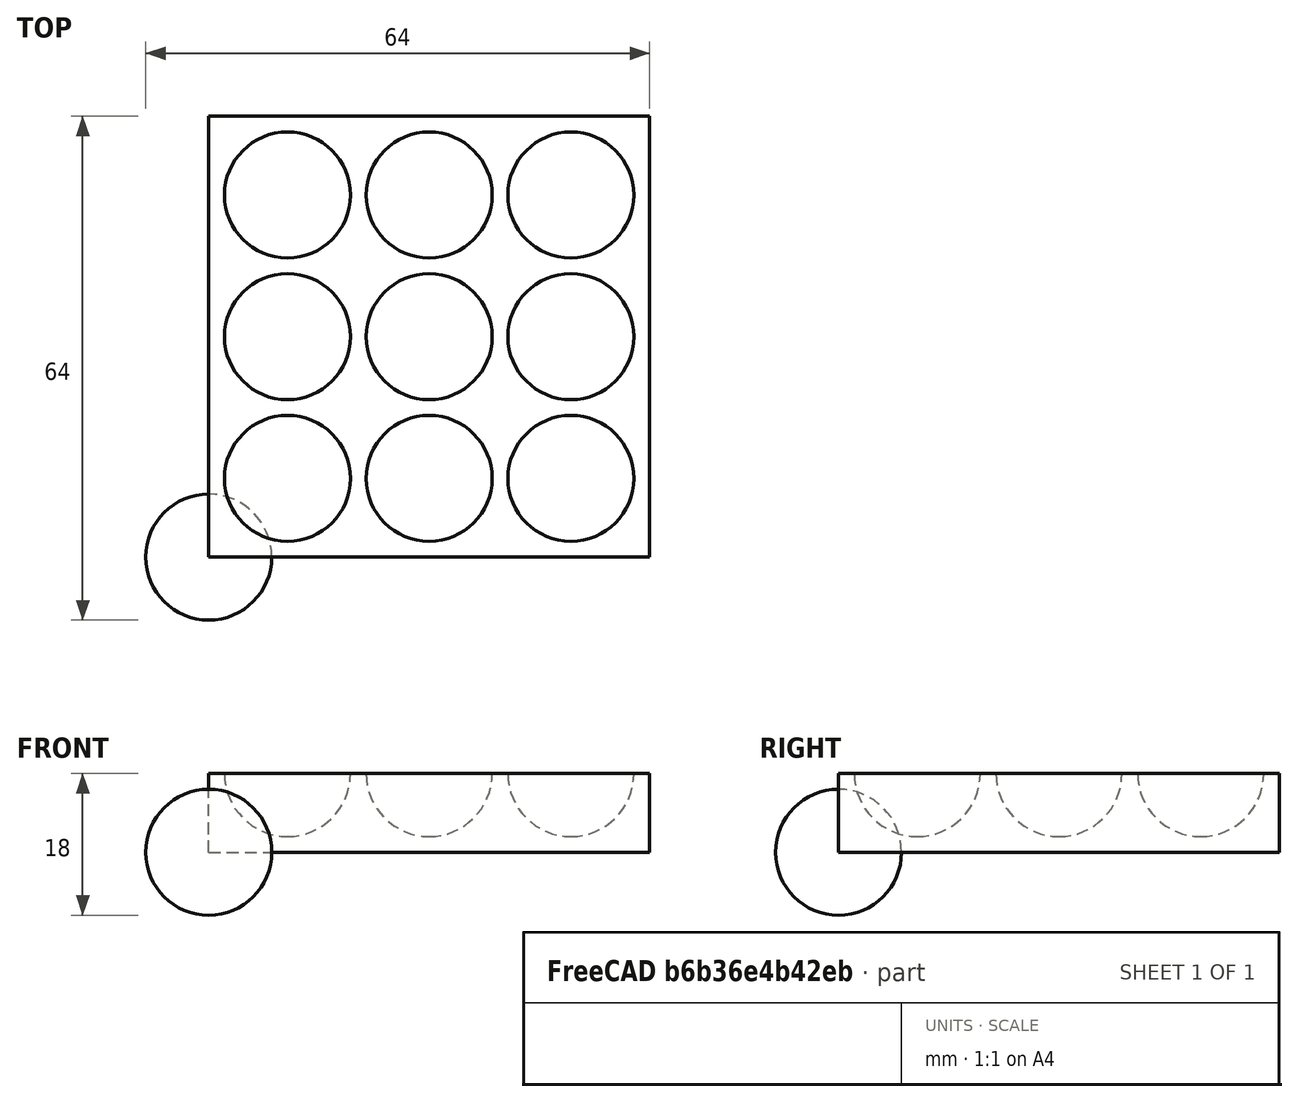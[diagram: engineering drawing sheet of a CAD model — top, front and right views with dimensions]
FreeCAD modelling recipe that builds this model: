
FCSTD DOCUMENT  (FreeCAD 0.21R33694 (Git))
Label: OJT1_T13P01_porta_canicas_
License: All rights reserved
LicenseURL: http://en.wikipedia.org/wiki/All_rights_reserved
objects: Part::Sphere×1, Part::FeaturePython×1, Part::Box×1, Part::Cut×1
note: 3 computed .brp shape members not serialized (recipe doc carries the construction recipe); baked Part::Feature solids carry a one-line shape summary decoded from their .brp

FEATURE [Part::Sphere] Sphere
  Angle1 = -90
  Angle2 = 90
  Angle3 = 360
  AttacherType = Attacher::AttachEngine3D
  Radius = 8
FEATURE [Part::FeaturePython] Array  # Draft array (typed FeaturePython)
  AlwaysSyncPlacement = false
  Angle = 360
  ArrayType = 0
  Axis = (0,0,1)
  Base = -> Sphere
  Center = (0,0,0)
  Count = 9
  ExpandArray = false
  Fuse = false
  IntervalAxis = (0,0,0)
  IntervalX = (18,0,0)
  IntervalY = (0,18,0)
  IntervalZ = (0,0,100)
  NumberCircles = 3
  NumberPolar = 5
  NumberX = 3
  NumberY = 3
  NumberZ = 1
  Placement = pos=(10,10,10) rot=(0,0,1;0rad)
  PlacementList = 9 placements: [(0,0,0),(0,18,0),(0,36,0),(18,0,0),(18,18,0),(18,36,0),(36,0,0),(36,18,0),(36,36,0)]
  RadialDistance = 50
  ScaleList = (9) [(1,1,1),(1,1,1),(1,1,1),(1,1,1),(1,1,1),(1,1,1),(1,1,1),(1,1,1),(1,1,1)]
  Symmetry = 1
  TangentialDistance = 25
FEATURE [Part::Box] Box  label="Cube"
  AttacherType = Attacher::AttachEngine3D
  Height = 10
  Length = 56
  Width = 56
FEATURE [Part::Cut] Cut
  Base = -> Box
  Refine = true
  Tool = -> Array
